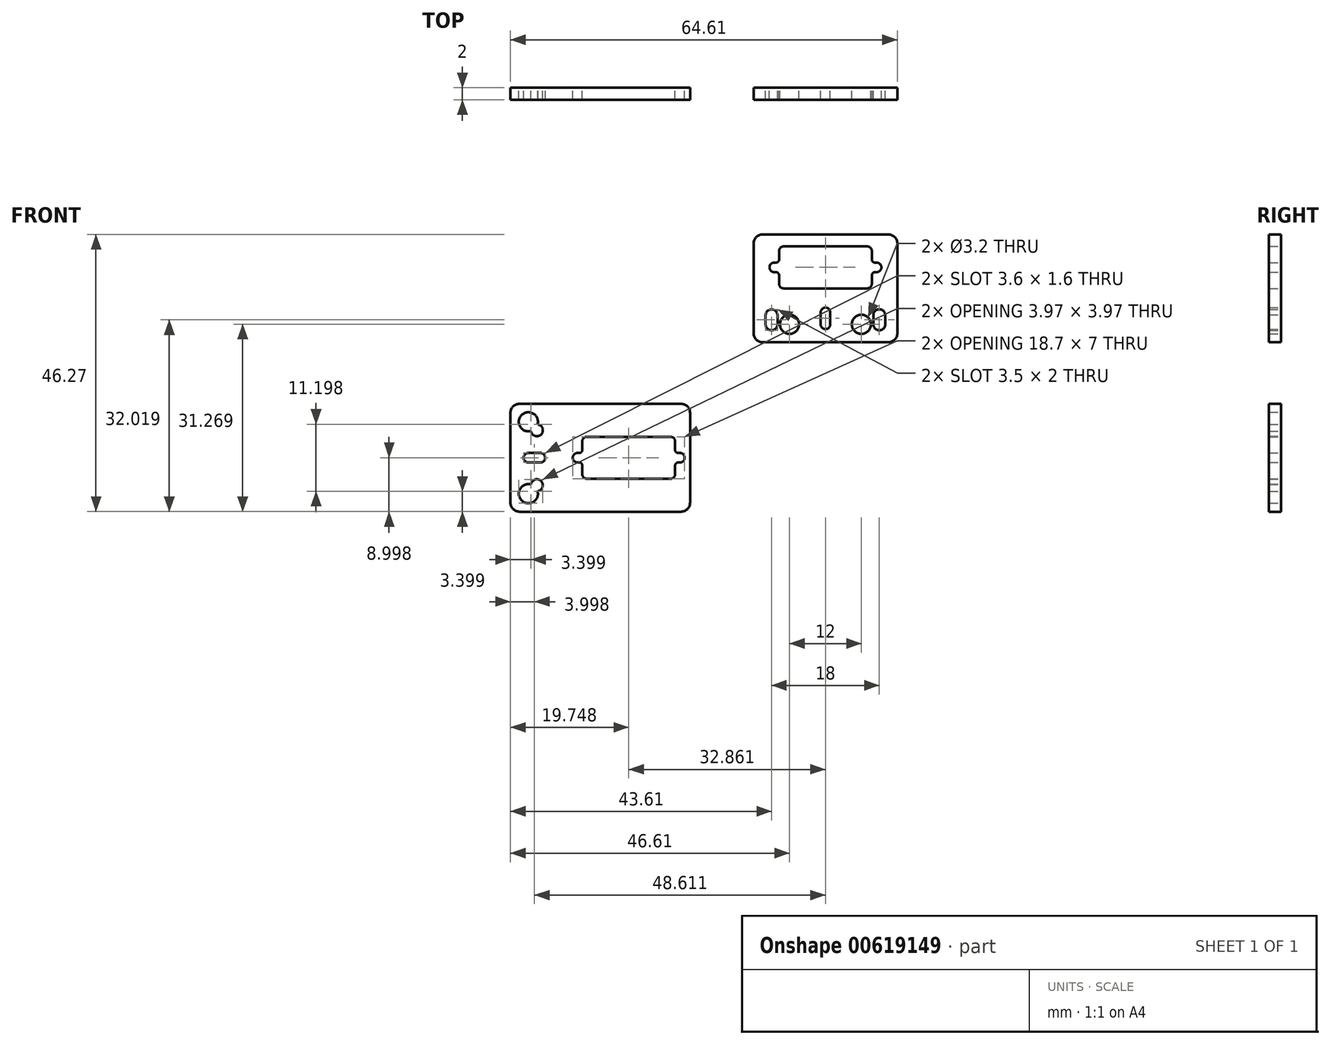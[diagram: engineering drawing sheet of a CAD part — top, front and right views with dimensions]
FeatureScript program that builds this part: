
annotation { "Feature Type Name" : "Feature", "Feature Type Description" : "" }
export const myFeature = defineFeature(function(context is Context, id is Id, definition is map)
    precondition{}
    {
        {
            var Q0;
            Q0=qCreatedBy(makeId("Front.planeOp"),FACE);
            var sketch = newSketch(context, id + "F0", { "sketchPlane" : qUnion([Q0])});
            skLineSegment(sketch, "E0.bottom", {"start": v(43.75, 49.95) * mm, "end": v(64.75, 49.95) * mm});
            skLineSegment(sketch, "E0.top", {"start": v(43.75, 31.95) * mm, "end": v(64.75, 31.95) * mm});
            skLineSegment(sketch, "E0.left", {"start": v(42.25, 48.45) * mm, "end": v(42.25, 33.45) * mm});
            skLineSegment(sketch, "E0.right", {"start": v(66.25, 48.45) * mm, "end": v(66.25, 33.45) * mm});
            skCircle(sketch, "E1", {"center": v(48.25, 34.95) * mm, "radius": 1.6 * mm});
            skLineSegment(sketch, "E2.bottom", {"start": v(47.25, 47.95) * mm, "end": v(61.25, 47.95) * mm});
            skLineSegment(sketch, "E2.top", {"start": v(47.25, 40.95) * mm, "end": v(61.25, 40.95) * mm});
            skLineSegment(sketch, "E2.left", {"start": v(46.5, 47.2) * mm, "end": v(46.5, 45.75) * mm});
            skLineSegment(sketch, "E2.right", {"start": v(62, 47.2) * mm, "end": v(62, 45.75) * mm});
            skArc(sketch, "E3", {"start": v(45.7, 45.25) * mm, "mid": v(44.9, 44.45) * mm, "end": v(45.7, 43.65) * mm});
            skLineSegment(sketch, "E4", {"start": v(46.5, 44.45) * mm, "end": v(62, 44.45) * mm, "construction": true});
            skLineSegment(sketch, "E5", {"start": v(54.25, 47.95) * mm, "end": v(54.25, 40.95) * mm, "construction": true});
            skLineSegment(sketch, "E6", {"start": v(45.7, 45.25) * mm, "end": v(46, 45.25) * mm});
            skLineSegment(sketch, "E7", {"start": v(45.7, 43.65) * mm, "end": v(46, 43.65) * mm});
            skLineSegment(sketch, "E8", {"start": v(54.25, 47.95) * mm, "end": v(54.25, 49.95) * mm, "construction": true});
            skPoint(sketch, "E8.endSnap0", {"position": v(54.25, 49.95) * mm});
            skLineSegment(sketch, "E9", {"start": v(54.25, 40.95) * mm, "end": v(54.25, 31.95) * mm, "construction": true});
            skLineSegment(sketch, "E10.trimOffspring", {"start": v(46.5, 43.15) * mm, "end": v(46.5, 41.7) * mm});
            skLineSegment(sketch, "E11.MirrorCS", {"start": v(62.8, 45.25) * mm, "end": v(62.5, 45.25) * mm});
            skArc(sketch, "E12.MirrorCS", {"start": v(62.8, 45.25) * mm, "mid": v(63.6, 44.45) * mm, "end": v(62.8, 43.65) * mm});
            skLineSegment(sketch, "E13.MirrorCS", {"start": v(62.8, 43.65) * mm, "end": v(62.5, 43.65) * mm});
            skLineSegment(sketch, "E14.trimOffspring", {"start": v(62, 43.15) * mm, "end": v(62, 41.7) * mm});
            skPoint(sketch, "E15.visualSharp", {"position": v(46.5, 45.25) * mm});
            skArc(sketch, "E15.filletArc", {"start": v(46, 45.25) * mm, "mid": v(46.35, 45.4) * mm, "end": v(46.5, 45.75) * mm});
            skPoint(sketch, "E16.visualSharp", {"position": v(46.5, 43.65) * mm});
            skArc(sketch, "E16.filletArc", {"start": v(46.5, 43.15) * mm, "mid": v(46.35, 43.5) * mm, "end": v(46, 43.65) * mm});
            skPoint(sketch, "E17.visualSharp", {"position": v(62, 45.25) * mm});
            skArc(sketch, "E17.filletArc", {"start": v(62, 45.75) * mm, "mid": v(62.15, 45.4) * mm, "end": v(62.5, 45.25) * mm});
            skPoint(sketch, "E18.visualSharp", {"position": v(62, 43.65) * mm});
            skArc(sketch, "E18.filletArc", {"start": v(62.5, 43.65) * mm, "mid": v(62.15, 43.5) * mm, "end": v(62, 43.15) * mm});
            skPoint(sketch, "E19.visualSharp", {"position": v(46.5, 47.95) * mm});
            skArc(sketch, "E19.filletArc", {"start": v(47.25, 47.95) * mm, "mid": v(46.72, 47.73) * mm, "end": v(46.5, 47.2) * mm});
            skPoint(sketch, "E20.visualSharp", {"position": v(62, 47.95) * mm});
            skArc(sketch, "E20.filletArc", {"start": v(62, 47.2) * mm, "mid": v(61.78, 47.73) * mm, "end": v(61.25, 47.95) * mm});
            skPoint(sketch, "E21.visualSharp", {"position": v(46.5, 40.95) * mm});
            skArc(sketch, "E21.filletArc", {"start": v(46.5, 41.7) * mm, "mid": v(46.72, 41.17) * mm, "end": v(47.25, 40.95) * mm});
            skPoint(sketch, "E22.visualSharp", {"position": v(62, 40.95) * mm});
            skArc(sketch, "E22.filletArc", {"start": v(61.25, 40.95) * mm, "mid": v(61.78, 41.17) * mm, "end": v(62, 41.7) * mm});
            skLineSegment(sketch, "E23", {"start": v(55.05, 36.95) * mm, "end": v(55.05, 34.95) * mm});
            skLineSegment(sketch, "E24", {"start": v(53.45, 36.95) * mm, "end": v(53.45, 34.95) * mm});
            skArc(sketch, "E25", {"start": v(53.45, 36.95) * mm, "mid": v(54.25, 36.15) * mm, "end": v(55.05, 36.95) * mm, "construction": true});
            skArc(sketch, "E26", {"start": v(55.05, 36.95) * mm, "mid": v(54.25, 37.75) * mm, "end": v(53.45, 36.95) * mm});
            skArc(sketch, "E27", {"start": v(53.45, 34.95) * mm, "mid": v(54.25, 34.15) * mm, "end": v(55.05, 34.95) * mm});
            skArc(sketch, "E28", {"start": v(55.05, 34.95) * mm, "mid": v(54.25, 35.75) * mm, "end": v(53.45, 34.95) * mm, "construction": true});
            skLineSegment(sketch, "E29", {"start": v(45.25, 36.45) * mm, "end": v(45.25, 34.95) * mm, "construction": true});
            skLineSegment(sketch, "E30", {"start": v(44.25, 36.45) * mm, "end": v(44.25, 34.95) * mm});
            skLineSegment(sketch, "E31", {"start": v(46.25, 36.45) * mm, "end": v(46.25, 34.95) * mm});
            skArc(sketch, "E32", {"start": v(44.25, 36.45) * mm, "mid": v(45.25, 35.45) * mm, "end": v(46.25, 36.45) * mm, "construction": true});
            skArc(sketch, "E33", {"start": v(46.25, 36.45) * mm, "mid": v(45.25, 37.45) * mm, "end": v(44.25, 36.45) * mm});
            skArc(sketch, "E34", {"start": v(44.25, 34.95) * mm, "mid": v(45.25, 33.95) * mm, "end": v(46.25, 34.95) * mm});
            skArc(sketch, "E35", {"start": v(46.25, 34.95) * mm, "mid": v(45.25, 35.95) * mm, "end": v(44.25, 34.95) * mm, "construction": true});
            skCircle(sketch, "E36.MirrorC", {"center": v(60.25, 34.95) * mm, "radius": 1.6 * mm});
            skArc(sketch, "E37.MirrorCS", {"start": v(62.25, 36.45) * mm, "mid": v(63.25, 37.45) * mm, "end": v(64.25, 36.45) * mm});
            skLineSegment(sketch, "E38.MirrorCS", {"start": v(62.25, 36.45) * mm, "end": v(62.25, 34.95) * mm});
            skArc(sketch, "E39.MirrorCS", {"start": v(64.25, 34.95) * mm, "mid": v(63.25, 33.95) * mm, "end": v(62.25, 34.95) * mm});
            skLineSegment(sketch, "E40.MirrorCS", {"start": v(64.25, 36.45) * mm, "end": v(64.25, 34.95) * mm});
            skLineSegment(sketch, "E41.bottom", {"start": v(3.14, 3.68) * mm, "end": v(30.14, 3.68) * mm});
            skLineSegment(sketch, "E41.top", {"start": v(3.14, 21.68) * mm, "end": v(30.14, 21.68) * mm});
            skLineSegment(sketch, "E41.left", {"start": v(1.64, 5.18) * mm, "end": v(1.64, 20.18) * mm});
            skLineSegment(sketch, "E41.right", {"start": v(31.64, 5.18) * mm, "end": v(31.64, 20.18) * mm});
            skLineSegment(sketch, "E42.bottom", {"start": v(14.39, 16.18) * mm, "end": v(28.39, 16.18) * mm});
            skLineSegment(sketch, "E42.top", {"start": v(14.39, 9.18) * mm, "end": v(28.39, 9.18) * mm});
            skLineSegment(sketch, "E42.left", {"start": v(13.64, 15.43) * mm, "end": v(13.64, 13.98) * mm});
            skLineSegment(sketch, "E42.right", {"start": v(29.14, 15.43) * mm, "end": v(29.14, 13.98) * mm});
            skLineSegment(sketch, "E43", {"start": v(13.64, 12.68) * mm, "end": v(29.14, 12.68) * mm, "construction": true});
            skLineSegment(sketch, "E44", {"start": v(21.39, 16.18) * mm, "end": v(21.39, 9.18) * mm, "construction": true});
            skLineSegment(sketch, "E45", {"start": v(31.64, 12.68) * mm, "end": v(29.14, 12.68) * mm, "construction": true});
            skLineSegment(sketch, "E46", {"start": v(29.94, 13.48) * mm, "end": v(29.64, 13.48) * mm});
            skLineSegment(sketch, "E47", {"start": v(29.94, 11.88) * mm, "end": v(29.64, 11.88) * mm});
            skArc(sketch, "E48", {"start": v(29.94, 13.48) * mm, "mid": v(29.14, 12.68) * mm, "end": v(29.94, 11.88) * mm, "construction": true});
            skArc(sketch, "E49", {"start": v(29.94, 11.88) * mm, "mid": v(30.74, 12.68) * mm, "end": v(29.94, 13.48) * mm});
            skLineSegment(sketch, "E50.trimOffspring", {"start": v(29.14, 11.38) * mm, "end": v(29.14, 9.93) * mm});
            skLineSegment(sketch, "E51.MirrorCS", {"start": v(12.84, 13.48) * mm, "end": v(13.14, 13.48) * mm});
            skArc(sketch, "E52.MirrorCS", {"start": v(12.84, 11.88) * mm, "mid": v(12.04, 12.68) * mm, "end": v(12.84, 13.48) * mm});
            skLineSegment(sketch, "E53.MirrorCS", {"start": v(12.84, 11.88) * mm, "end": v(13.14, 11.88) * mm});
            skLineSegment(sketch, "E54.trimOffspring", {"start": v(13.64, 11.38) * mm, "end": v(13.64, 9.93) * mm});
            skPoint(sketch, "E55.visualSharp", {"position": v(13.64, 13.48) * mm});
            skArc(sketch, "E55.filletArc", {"start": v(13.14, 13.48) * mm, "mid": v(13.5, 13.62) * mm, "end": v(13.64, 13.98) * mm});
            skPoint(sketch, "E56.visualSharp", {"position": v(13.64, 11.88) * mm});
            skArc(sketch, "E56.filletArc", {"start": v(13.64, 11.38) * mm, "mid": v(13.5, 11.73) * mm, "end": v(13.14, 11.88) * mm});
            skPoint(sketch, "E57.visualSharp", {"position": v(29.14, 11.88) * mm});
            skArc(sketch, "E57.filletArc", {"start": v(29.64, 11.88) * mm, "mid": v(29.28, 11.73) * mm, "end": v(29.14, 11.38) * mm});
            skPoint(sketch, "E58.visualSharp", {"position": v(29.14, 13.48) * mm});
            skArc(sketch, "E58.filletArc", {"start": v(29.14, 13.98) * mm, "mid": v(29.28, 13.62) * mm, "end": v(29.64, 13.48) * mm});
            skPoint(sketch, "E59.visualSharp", {"position": v(13.64, 16.18) * mm});
            skArc(sketch, "E59.filletArc", {"start": v(14.39, 16.18) * mm, "mid": v(13.86, 15.96) * mm, "end": v(13.64, 15.43) * mm});
            skPoint(sketch, "E60.visualSharp", {"position": v(13.64, 9.18) * mm});
            skArc(sketch, "E60.filletArc", {"start": v(13.64, 9.93) * mm, "mid": v(13.86, 9.4) * mm, "end": v(14.39, 9.18) * mm});
            skPoint(sketch, "E61.visualSharp", {"position": v(29.14, 16.18) * mm});
            skArc(sketch, "E61.filletArc", {"start": v(29.14, 15.43) * mm, "mid": v(28.92, 15.96) * mm, "end": v(28.39, 16.18) * mm});
            skPoint(sketch, "E62.visualSharp", {"position": v(29.14, 9.18) * mm});
            skArc(sketch, "E62.filletArc", {"start": v(28.39, 9.18) * mm, "mid": v(28.92, 9.4) * mm, "end": v(29.14, 9.93) * mm});
            skLineSegment(sketch, "E63", {"start": v(1.64, 12.68) * mm, "end": v(12.04, 12.68) * mm, "construction": true});
            skLineSegment(sketch, "E64", {"start": v(4.64, 11.88) * mm, "end": v(6.64, 11.88) * mm});
            skLineSegment(sketch, "E65", {"start": v(4.64, 13.48) * mm, "end": v(6.64, 13.48) * mm});
            skArc(sketch, "E66", {"start": v(4.64, 13.48) * mm, "mid": v(3.84, 12.68) * mm, "end": v(4.64, 11.88) * mm});
            skArc(sketch, "E67", {"start": v(4.64, 11.88) * mm, "mid": v(5.44, 12.68) * mm, "end": v(4.64, 13.48) * mm, "construction": true});
            skArc(sketch, "E68", {"start": v(6.64, 13.48) * mm, "mid": v(5.84, 12.68) * mm, "end": v(6.64, 11.88) * mm, "construction": true});
            skArc(sketch, "E69", {"start": v(6.64, 11.88) * mm, "mid": v(7.44, 12.68) * mm, "end": v(6.64, 13.48) * mm});
            skArc(sketch, "E70", {"start": v(6.18, 18.26) * mm, "mid": v(3.5, 19.8) * mm, "end": v(5.06, 17.14) * mm});
            skArc(sketch, "E71", {"start": v(5.06, 17.14) * mm, "mid": v(6.76, 16.56) * mm, "end": v(6.18, 18.26) * mm});
            skLineSegment(sketch, "E72", {"start": v(1.64, 21.68) * mm, "end": v(10.64, 12.68) * mm, "construction": true});
            skArc(sketch, "E73.MirrorCS", {"start": v(5.06, 8.22) * mm, "mid": v(6.76, 8.8) * mm, "end": v(6.18, 7.1) * mm});
            skArc(sketch, "E74.MirrorCS", {"start": v(6.18, 7.1) * mm, "mid": v(3.5, 5.55) * mm, "end": v(5.06, 8.22) * mm});
            skPoint(sketch, "E75.visualSharp", {"position": v(1.64, 21.68) * mm});
            skArc(sketch, "E75.filletArc", {"start": v(3.14, 21.68) * mm, "mid": v(2.08, 21.24) * mm, "end": v(1.64, 20.18) * mm});
            skPoint(sketch, "E76.visualSharp", {"position": v(1.64, 3.68) * mm});
            skArc(sketch, "E76.filletArc", {"start": v(1.64, 5.18) * mm, "mid": v(2.08, 4.12) * mm, "end": v(3.14, 3.68) * mm});
            skPoint(sketch, "E77.visualSharp", {"position": v(31.64, 3.68) * mm});
            skArc(sketch, "E77.filletArc", {"start": v(30.14, 3.68) * mm, "mid": v(31.2, 4.12) * mm, "end": v(31.64, 5.18) * mm});
            skPoint(sketch, "E78.visualSharp", {"position": v(31.64, 21.68) * mm});
            skArc(sketch, "E78.filletArc", {"start": v(31.64, 20.18) * mm, "mid": v(31.2, 21.24) * mm, "end": v(30.14, 21.68) * mm});
            skPoint(sketch, "E79.visualSharp", {"position": v(42.25, 31.95) * mm});
            skArc(sketch, "E79.filletArc", {"start": v(42.25, 33.45) * mm, "mid": v(42.69, 32.39) * mm, "end": v(43.75, 31.95) * mm});
            skPoint(sketch, "E80.visualSharp", {"position": v(42.25, 49.95) * mm});
            skArc(sketch, "E80.filletArc", {"start": v(43.75, 49.95) * mm, "mid": v(42.69, 49.5) * mm, "end": v(42.25, 48.45) * mm});
            skPoint(sketch, "E81.visualSharp", {"position": v(66.25, 49.95) * mm});
            skArc(sketch, "E81.filletArc", {"start": v(66.25, 48.45) * mm, "mid": v(65.81, 49.5) * mm, "end": v(64.75, 49.95) * mm});
            skPoint(sketch, "E82.visualSharp", {"position": v(66.25, 31.95) * mm});
            skArc(sketch, "E82.filletArc", {"start": v(64.75, 31.95) * mm, "mid": v(65.81, 32.39) * mm, "end": v(66.25, 33.45) * mm});
            skSolve(sketch);
        }
        {
            var Q0;
            Q0=makeQuery(id+"F0.imprint","IMPRINT",FACE,{"disambiguationData":[TD([[makeQuery(id+"F0.imprint","IMPRINT",EDGE,{"derivedFrom":sQuery(id+"F0.wireOp",EDGE,"E0.bottom")}),-1.0]])]});
            extrude(context, id + "F1", {"entities" : qUnion([Q0]), "depth" : 2 * mm, "offsetDistance" : 25 * mm});
        }
        {
            var Q0;
            Q0=makeQuery(id+"F0.imprint","IMPRINT",FACE,{"disambiguationData":[TD([[makeQuery(id+"F0.imprint","IMPRINT",EDGE,{"derivedFrom":sQuery(id+"F0.wireOp",EDGE,"E41.bottom")}),1.0]])]});
            extrude(context, id + "F2", {"entities" : qUnion([Q0]), "depth" : 2 * mm, "offsetDistance" : 25 * mm});
        }
    });
